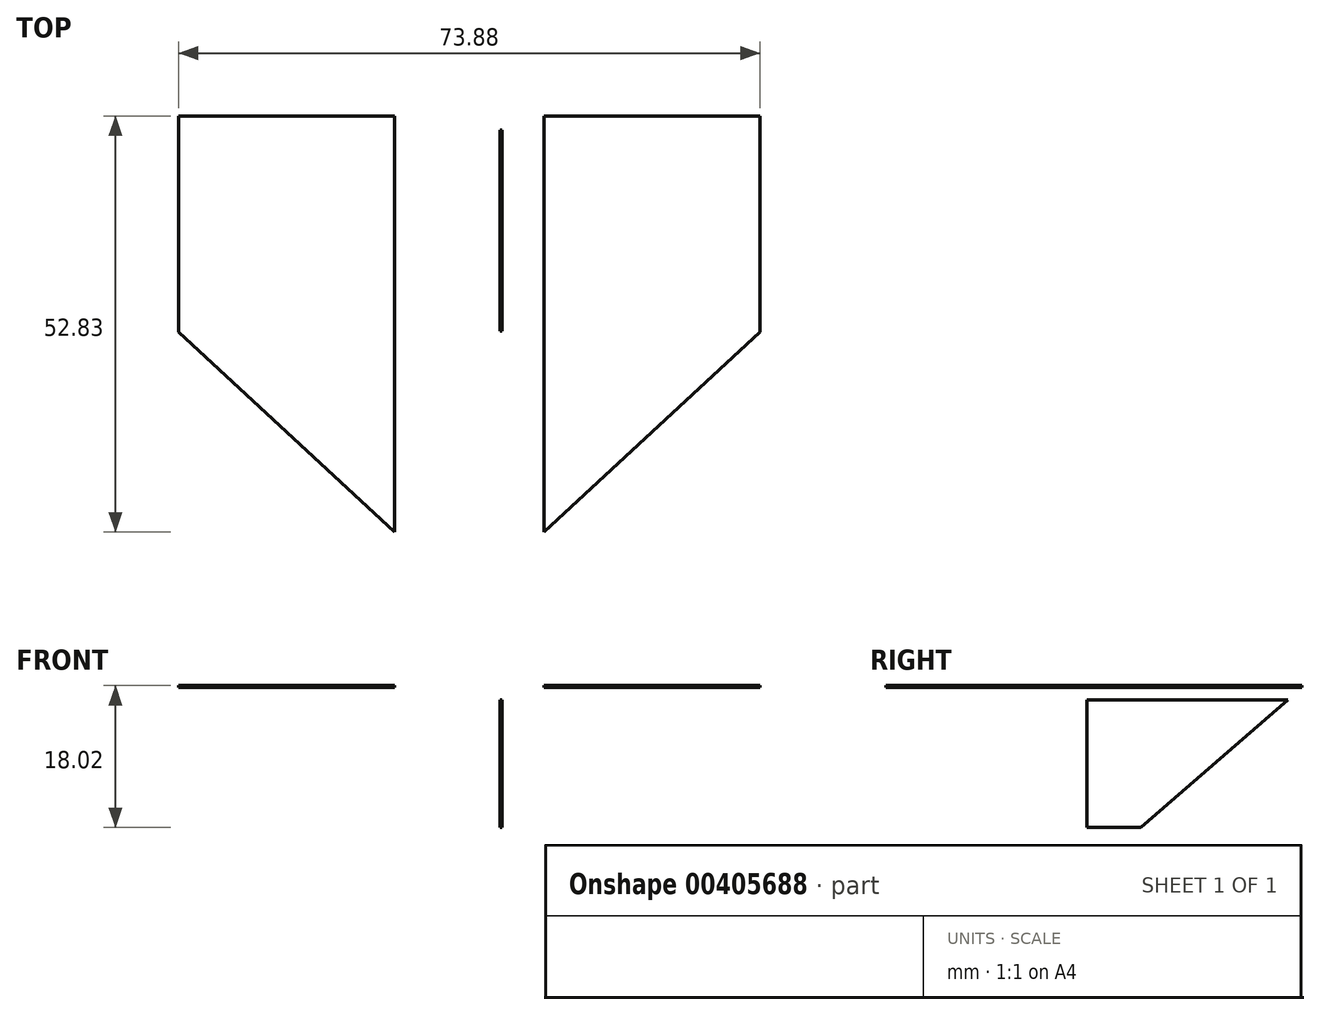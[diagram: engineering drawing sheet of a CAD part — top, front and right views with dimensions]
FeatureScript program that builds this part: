
annotation { "Feature Type Name" : "Feature", "Feature Type Description" : "" }
export const myFeature = defineFeature(function(context is Context, id is Id, definition is map)
    precondition{}
    {
        {
            var Q0;
            Q0=qCreatedBy(makeId("Top.planeOp"),FACE);
            var sketch = newSketch(context, id + "F0", { "sketchPlane" : qUnion([Q0])});
            skLineSegment(sketch, "E0.bottom", {"start": v(-40.86, 21.89) * mm, "end": v(-13.43, 21.89) * mm});
            skLineSegment(sketch, "E0.top", {"start": v(-40.86, -5.54) * mm, "end": v(-13.43, -5.54) * mm});
            skLineSegment(sketch, "E0.left", {"start": v(-40.86, 21.89) * mm, "end": v(-40.86, -5.54) * mm});
            skLineSegment(sketch, "E0.right", {"start": v(-13.43, 21.89) * mm, "end": v(-13.43, -5.54) * mm});
            skLineSegment(sketch, "E1.bottom", {"start": v(5.59, 21.89) * mm, "end": v(33.02, 21.89) * mm});
            skLineSegment(sketch, "E1.top", {"start": v(5.59, -5.54) * mm, "end": v(33.02, -5.54) * mm});
            skLineSegment(sketch, "E1.left", {"start": v(5.59, 21.89) * mm, "end": v(5.59, -5.54) * mm});
            skLineSegment(sketch, "E1.right", {"start": v(33.02, 21.89) * mm, "end": v(33.02, -5.54) * mm});
            skLineSegment(sketch, "E2", {"start": v(-13.43, -5.54) * mm, "end": v(-13.43, -30.94) * mm});
            skLineSegment(sketch, "E3", {"start": v(-13.43, -30.94) * mm, "end": v(-40.86, -5.54) * mm});
            skLineSegment(sketch, "E4", {"start": v(5.59, -5.54) * mm, "end": v(5.59, -30.94) * mm});
            skLineSegment(sketch, "E5", {"start": v(5.59, -30.94) * mm, "end": v(33.02, -5.54) * mm});
            skLineSegment(sketch, "E6.top", {"start": v(19.05, -18.24) * mm, "end": v(19.3, -18.24) * mm});
            skSolve(sketch);
        }
        {
            var Q0;
            Q0 = qSketchRegion(id + "F0", true);
            extrude(context, id + "F1", {"entities" : qUnion([Q0]), "oppositeDirection" : true, "depth" : 0.25 * mm});
        }
        {
            var Q0;
            Q0=qCreatedBy(makeId("Right.planeOp"),FACE);
            var sketch = newSketch(context, id + "F2", { "sketchPlane" : qUnion([Q0])});
            skLineSegment(sketch, "E7", {"start": v(-5.39, -1.84) * mm, "end": v(20.13, -1.84) * mm});
            skLineSegment(sketch, "E8", {"start": v(-5.39, -1.84) * mm, "end": v(-5.39, -18.02) * mm});
            skLineSegment(sketch, "E9", {"start": v(-5.39, -18.02) * mm, "end": v(1.47, -18.02) * mm});
            skLineSegment(sketch, "E10", {"start": v(1.47, -18.02) * mm, "end": v(20.13, -1.84) * mm});
            skSolve(sketch);
        }
        {
            var Q0;
            Q0 = qSketchRegion(id + "F2", true);
            extrude(context, id + "F3", {"entities" : qUnion([Q0]), "depth" : 0.25 * mm});
        }
    });
